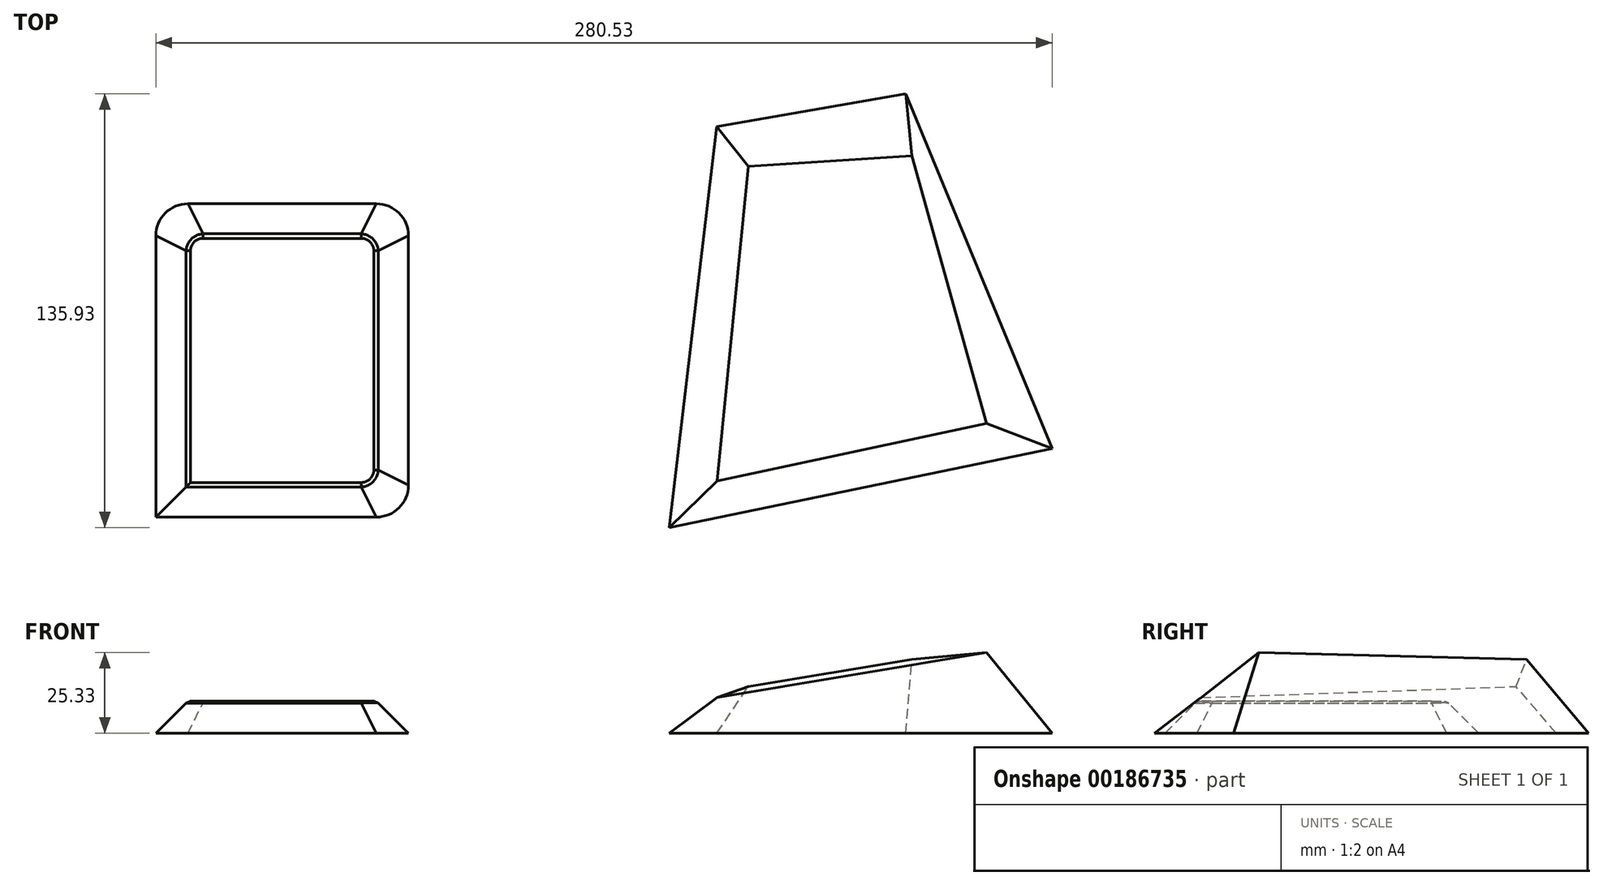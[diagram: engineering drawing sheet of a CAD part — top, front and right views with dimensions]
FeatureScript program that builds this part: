
annotation { "Feature Type Name" : "Feature", "Feature Type Description" : "" }
export const myFeature = defineFeature(function(context is Context, id is Id, definition is map)
    precondition{}
    {
        {
            var Q0;
            Q0=qCreatedBy(makeId("Top.planeOp"),FACE);
            cPlane(context, id + "F0", {"entities" : qUnion([Q0]), "cplaneType" : CPlaneType.OFFSET, "offset" : 10 * mm, "width" : 152.4 * mm, "height" : 152.4 * mm});
        }
        {
            var Q0;
            Q0=qCreatedBy(makeId("Top.planeOp"),FACE);
            var sketch = newSketch(context, id + "F1", { "sketchPlane" : qUnion([Q0])});
            skLineSegment(sketch, "E0.bottom", {"start": v(-29.51, 49.07) * mm, "end": v(29.51, 49.07) * mm});
            skLineSegment(sketch, "E0.top", {"start": v(-39.51, -49.07) * mm, "end": v(29.51, -49.07) * mm});
            skLineSegment(sketch, "E0.left", {"start": v(-39.51, 39.07) * mm, "end": v(-39.51, -49.07) * mm});
            skLineSegment(sketch, "E0.right", {"start": v(39.51, 39.07) * mm, "end": v(39.51, -39.07) * mm});
            skPoint(sketch, "E0.middle", {"position": v(0, 0) * mm});
            skPoint(sketch, "E1.visualSharp", {"position": v(-39.51, 49.07) * mm});
            skArc(sketch, "E1.filletArc", {"start": v(-29.51, 49.07) * mm, "mid": v(-36.59, 46.14) * mm, "end": v(-39.51, 39.07) * mm});
            skPoint(sketch, "E2.visualSharp", {"position": v(39.51, 49.07) * mm});
            skArc(sketch, "E2.filletArc", {"start": v(39.51, 39.07) * mm, "mid": v(36.59, 46.14) * mm, "end": v(29.51, 49.07) * mm});
            skPoint(sketch, "E3.visualSharp", {"position": v(39.51, -49.07) * mm});
            skArc(sketch, "E3.filletArc", {"start": v(29.51, -49.07) * mm, "mid": v(36.59, -46.14) * mm, "end": v(39.51, -39.07) * mm});
            skPoint(sketch, "E4.visualSharp", {"position": v(-39.51, -49.07) * mm});
            skSolve(sketch);
        }
        {
            var Q0;
            Q0=qCreatedBy(id+"F0.planeOp",FACE);
            var sketch = newSketch(context, id + "F2", { "sketchPlane" : qUnion([Q0])});
            skLineSegment(sketch, "E5.bottom", {"start": v(-24.51, 39.07) * mm, "end": v(24.51, 39.07) * mm});
            skLineSegment(sketch, "E5.top", {"start": v(-29.51, -39.07) * mm, "end": v(24.51, -39.07) * mm});
            skLineSegment(sketch, "E5.left", {"start": v(-29.51, 34.07) * mm, "end": v(-29.51, -39.07) * mm});
            skLineSegment(sketch, "E5.right", {"start": v(29.51, 34.07) * mm, "end": v(29.51, -34.07) * mm});
            skPoint(sketch, "E5.middle", {"position": v(0, 0) * mm});
            skPoint(sketch, "E6.visualSharp", {"position": v(-29.51, -39.07) * mm});
            skPoint(sketch, "E7.visualSharp", {"position": v(-29.51, 39.07) * mm});
            skArc(sketch, "E7.filletArc", {"start": v(-24.51, 39.07) * mm, "mid": v(-28.05, 37.6) * mm, "end": v(-29.51, 34.07) * mm});
            skPoint(sketch, "E8.visualSharp", {"position": v(29.51, 39.07) * mm});
            skArc(sketch, "E8.filletArc", {"start": v(29.51, 34.07) * mm, "mid": v(28.05, 37.6) * mm, "end": v(24.51, 39.07) * mm});
            skPoint(sketch, "E9.visualSharp", {"position": v(29.51, -39.07) * mm});
            skArc(sketch, "E9.filletArc", {"start": v(24.51, -39.07) * mm, "mid": v(28.05, -37.6) * mm, "end": v(29.51, -34.07) * mm});
            skSolve(sketch);
        }
        {
            var Q0;
            Q0=makeQuery(id+"F1.imprint","IMPRINT",FACE,{"disambiguationData":[TD([[makeQuery(id+"F1.imprint","IMPRINT",EDGE,{"derivedFrom":sQuery(id+"F1.wireOp",EDGE,"E0.bottom")}),-1.0]])]});
            var Q1;
            Q1=makeQuery(id+"F2.imprint","IMPRINT",FACE,{"disambiguationData":[TD([[makeQuery(id+"F2.imprint","IMPRINT",EDGE,{"derivedFrom":sQuery(id+"F2.wireOp",EDGE,"E5.bottom")}),-1.0]])]});
            loft(context, id + "F3", {"sheetProfilesArray" : [{ "sheetProfileEntities" : qUnion([Q0]) }, { "sheetProfileEntities" : qUnion([Q1]) }]});
        }
        {
            var Q0;
            Q0=makeQuery(id+"F3.opLoft","MID_CAP_EDGE",EDGE,{"disambiguationData":[OSD([sQuery(id+"F2.wireOp",EDGE,"E5.left"),sQuery(id+"F2.wireOp",EDGE,"E6.filletArc"),sQuery(id+"F2.wireOp",EDGE,"E7.filletArc")])],"capPos":1.0});
            chamfer(context, id + "F4", {"entities" : qUnion([Q0]), "width" : 2 * mm, "tangentPropagation" : true});
        }
        {
            var Q0;
            Q0=qCreatedBy(makeId("Top.planeOp"),FACE);
            var sketch = newSketch(context, id + "F5", { "sketchPlane" : qUnion([Q0])});
            skPoint(sketch, "E10", {"position": v(70, -54.43) * mm});
            skPoint(sketch, "E11", {"position": v(56.43, 64.76) * mm});
            skSolve(sketch);
        }
        {
            var Q0;
            Q0=qCreatedBy(id+"F0.planeOp",FACE);
            var sketch = newSketch(context, id + "F6", { "sketchPlane" : qUnion([Q0])});
            skPoint(sketch, "E12", {"position": v(124.77, 0) * mm});
            skSolve(sketch);
        }
        {
            var Q0;
            Q0=sQuery(id+"F5.wireOp",VERTEX,"E11");
            var Q1;
            Q1=sQuery(id+"F6.wireOp",VERTEX,"E12");
            var Q2;
            Q2=sQuery(id+"F5.wireOp",VERTEX,"E10");
            cPlane(context, id + "F7", {"entities" : qUnion([Q0, Q1, Q2]), "cplaneType" : CPlaneType.THREE_POINT, "offset" : 25 * mm, "width" : 150 * mm, "height" : 150 * mm});
        }
        {
            var Q0;
            Q0=qCreatedBy(id+"F7.planeOp",FACE);
            var sketch = newSketch(context, id + "F8", { "sketchPlane" : qUnion([Q0])});
            skLineSegment(sketch, "E13", {"start": v(136.21, -37.53) * mm, "end": v(146.16, 61.08) * mm});
            skLineSegment(sketch, "E14", {"start": v(146.16, 61.08) * mm, "end": v(198.08, 64.5) * mm});
            skLineSegment(sketch, "E15", {"start": v(198.08, 64.5) * mm, "end": v(221.7, -19.24) * mm});
            skLineSegment(sketch, "E16", {"start": v(221.7, -19.24) * mm, "end": v(136.21, -37.53) * mm});
            skSolve(sketch);
        }
        {
            var Q0;
            Q0=qCreatedBy(makeId("Top.planeOp"),FACE);
            var sketch = newSketch(context, id + "F9", { "sketchPlane" : qUnion([Q0])});
            skLineSegment(sketch, "E17", {"start": v(136.06, 73.3) * mm, "end": v(195.25, 83.51) * mm});
            skLineSegment(sketch, "E18", {"start": v(195.25, 83.51) * mm, "end": v(241.02, -27.6) * mm});
            skLineSegment(sketch, "E19", {"start": v(241.02, -27.6) * mm, "end": v(121.13, -52.42) * mm});
            skLineSegment(sketch, "E20", {"start": v(121.13, -52.42) * mm, "end": v(136.06, 73.3) * mm});
            skSolve(sketch);
        }
        {
            var Q0;
            Q0=makeQuery(id+"F9.imprint","IMPRINT",FACE,{"disambiguationData":[TD([[makeQuery(id+"F9.imprint","IMPRINT",EDGE,{"derivedFrom":sQuery(id+"F9.wireOp",EDGE,"E17")}),-1.0]])]});
            var Q1;
            Q1=makeQuery(id+"F8.imprint","IMPRINT",FACE,{"disambiguationData":[TD([[makeQuery(id+"F8.imprint","IMPRINT",EDGE,{"derivedFrom":sQuery(id+"F8.wireOp",EDGE,"E13")}),-1.0]])]});
            loft(context, id + "F10", {"sheetProfilesArray" : [{ "sheetProfileEntities" : qUnion([Q0]) }, { "sheetProfileEntities" : qUnion([Q1]) }]});
        }
    });
